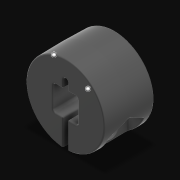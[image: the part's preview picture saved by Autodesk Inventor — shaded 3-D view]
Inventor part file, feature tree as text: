
AUTODESK INVENTOR PART (.ipt)
format: ipt  version: 2021 (Build 250183000, 183)  size: 481,280 bytes
history: native  units: in
note: dims shown in document units (in); Inventor stores cm internally (conversion verified against a paired STEP export)
features: fillet x1, other x1, imported_body x1
ambient origin geometry x8: Origin, YZ Plane, XZ Plane, XY Plane, X Axis, Y Axis, Z Axis, Center Point
bodies: Body1 (feature_tree)
feature tree (3):
  fillet  "Fillet4"  [1 undecoded]
  other  "276-3520-STEP1"
  imported_body  "Base1"
note: 1 required parameter value undecoded (feature->parameter linkage not recoverable at this tier; creation-order binding heuristic only, values carry confidence <= 0.55)
